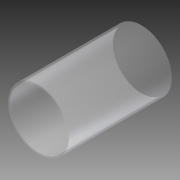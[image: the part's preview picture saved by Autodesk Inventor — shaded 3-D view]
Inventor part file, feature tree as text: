
AUTODESK INVENTOR PART (.ipt)
format: ipt  version: 2015 (Build 190159000, 159)  size: 84,480 bytes
history: native  units: mm
features: extrude x1, sketch x1
ambient origin geometry x8: Origin, YZ Plane, XZ Plane, XY Plane, X Axis, Y Axis, Z Axis, Center Point
bodies: Solid1 (feature_tree)
feature tree (2):
  extrude  "Extrusion1"  Depth=180.0mm
  sketch  "Sketch1"  dims[d0=106.0mm d1=100.0mm d2=180.0mm d3=0.0mm]
